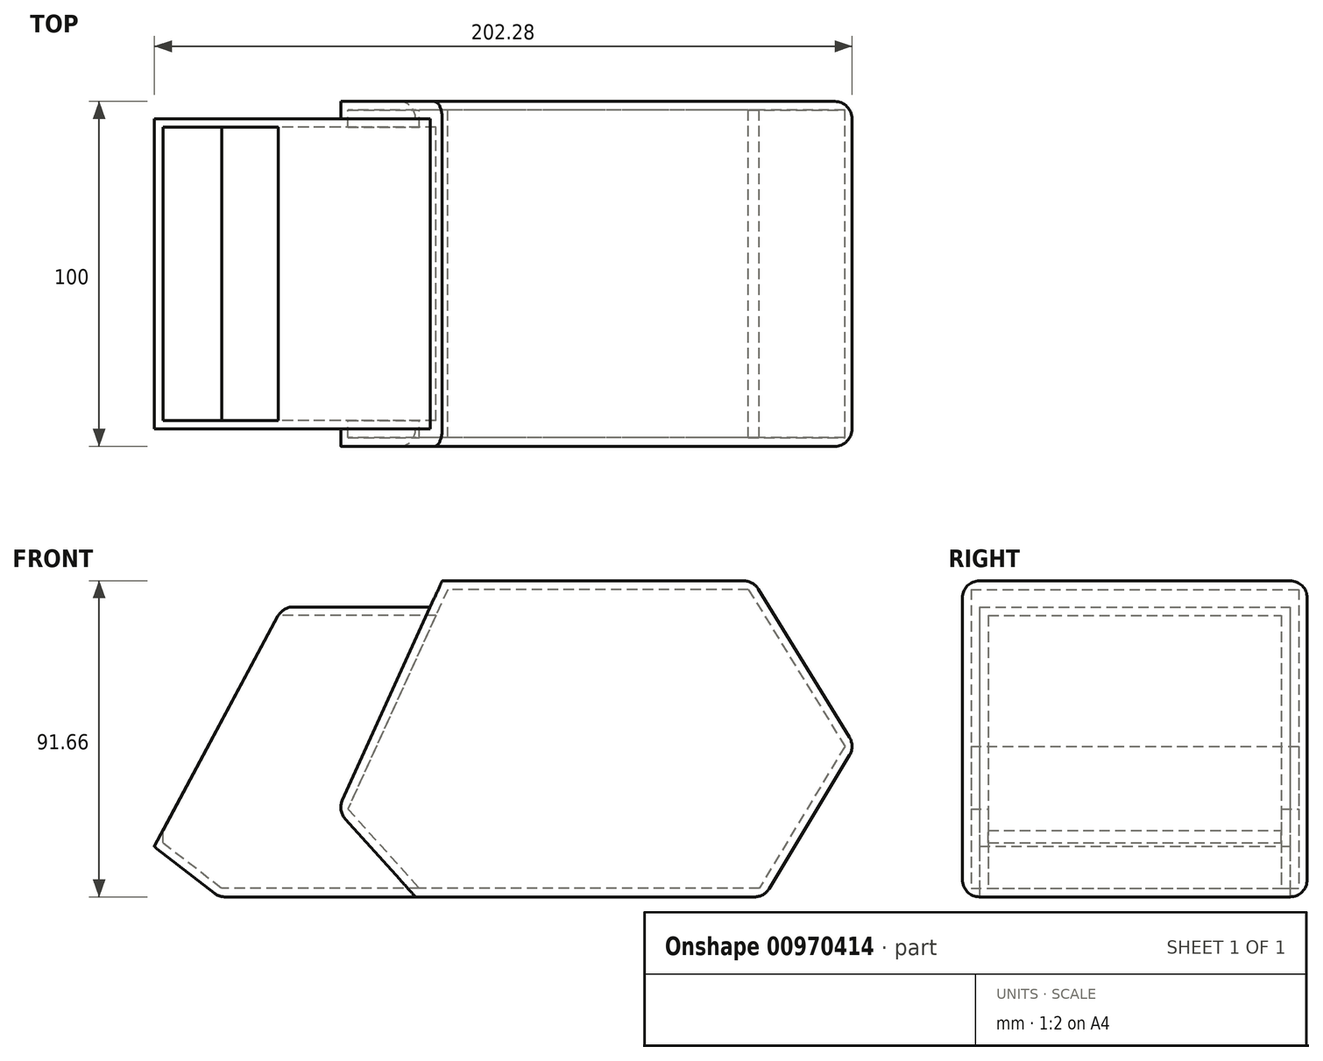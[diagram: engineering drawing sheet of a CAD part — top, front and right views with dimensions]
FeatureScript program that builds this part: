
annotation { "Feature Type Name" : "Feature", "Feature Type Description" : "" }
export const myFeature = defineFeature(function(context is Context, id is Id, definition is map)
    precondition{}
    {
        {
            var Q0;
            Q0=qCreatedBy(makeId("Front.planeOp"),FACE);
            var sketch = newSketch(context, id + "F0", { "sketchPlane" : qUnion([Q0])});
            skLineSegment(sketch, "E0.bottom", {"start": v(74.72, -45.83) * mm, "end": v(-83.37, -45.83) * mm});
            skLineSegment(sketch, "E0.top", {"start": v(71.54, 45.83) * mm, "end": v(-18.63, 45.83) * mm});
            skLineSegment(sketch, "E0.right", {"start": v(-102.1, -31.3) * mm, "end": v(-102.1, -31.17) * mm});
            skPoint(sketch, "E0.middle", {"position": v(0, 0) * mm});
            skLineSegment(sketch, "E1", {"start": v(-18.63, 45.83) * mm, "end": v(-48.93, -20.8) * mm});
            skLineSegment(sketch, "E2", {"start": v(-48.93, -20.8) * mm, "end": v(-26.37, -45.83) * mm});
            skLineSegment(sketch, "E3", {"start": v(71.54, 45.83) * mm, "end": v(101.05, -2.12) * mm});
            skLineSegment(sketch, "E4", {"start": v(101.05, -2.12) * mm, "end": v(74.72, -45.83) * mm});
            skPoint(sketch, "E5.orphan", {"position": v(102.1, 45.83) * mm});
            skPoint(sketch, "E6.orphan", {"position": v(102.1, -45.83) * mm});
            skLineSegment(sketch, "E7", {"start": v(-22.08, 38.24) * mm, "end": v(-64.83, 38.24) * mm});
            skPoint(sketch, "E8.orphan", {"position": v(-102.1, 45.83) * mm});
            skLineSegment(sketch, "E9", {"start": v(-64.83, 38.24) * mm, "end": v(-102.14, -31.27) * mm});
            skLineSegment(sketch, "E10", {"start": v(-102.14, -31.27) * mm, "end": v(-83.37, -45.83) * mm});
            skPoint(sketch, "E11.orphan", {"position": v(-102.1, -45.83) * mm});
            skSolve(sketch);
        }
        {
            var Q0;
            {var subQ1=sQuery(id+"F0.wireOp",EDGE,"E0.top");Q0=makeQuery(id+"F0.imprint","IMPRINT",FACE,{"disambiguationData":[TD([[makeQuery(id+"F0.imprint","IMPRINT",EDGE,{"derivedFrom":subQ1}),1.0]])]});}
            extrude(context, id + "F1", {"entities" : qUnion([Q0]), "depth" : 50 * mm, "offsetDistance" : 25 * mm, "hasSecondDirection" : true, "secondDirectionOppositeDirection" : true, "secondDirectionDepth" : 50 * mm});
        }
        {
            var Q0;
            {var subQ3=sQuery(id+"F0.wireOp",EDGE,"E0.right");Q0=makeQuery(id+"F0.imprint","IMPRINT",FACE,{"disambiguationData":[TD([[makeQuery(id+"F0.imprint","IMPRINT",EDGE,{"derivedFrom":subQ3}),-1.0]])]});}
            extrude(context, id + "F2", {"entities" : qUnion([Q0]), "operationType" : NewBodyOperationType.ADD, "depth" : 45 * mm, "offsetDistance" : 25 * mm, "hasSecondDirection" : true, "secondDirectionOppositeDirection" : true, "secondDirectionDepth" : 45 * mm});
        }
        {
            var Q0;
            Q0=makeQuery(id+"F2.opExtrude","SWEPT_FACE",FACE,{"disambiguationData":[OSD([sQuery(id+"F0.wireOp",EDGE,"E9")])]});
            shell(context, id + "F3", {"entities" : qUnion([Q0]), "thickness" : 2.5 * mm});
        }
        {
            var Q0;
            Q0=makeQuery(id+"F1.opExtrude","CAP_EDGE",EDGE,{"disambiguationData":[OSD([sQuery(id+"F0.wireOp",EDGE,"E0.top")])],"isStart":false});
            var Q1;
            Q1=makeQuery(id+"F1.opExtrude","CAP_EDGE",EDGE,{"disambiguationData":[OSD([sQuery(id+"F0.wireOp",EDGE,"E0.bottom")])],"isStart":false});
            var Q2;
            Q2=makeQuery(id+"F1.opExtrude","CAP_EDGE",EDGE,{"disambiguationData":[OSD([sQuery(id+"F0.wireOp",EDGE,"E0.top")])],"isStart":true});
            var Q3;
            Q3=makeQuery(id+"F1.opExtrude","CAP_EDGE",EDGE,{"disambiguationData":[OSD([sQuery(id+"F0.wireOp",EDGE,"E0.bottom")])],"isStart":true});
            var Q4;
            Q4=makeQuery(id+"F1.opExtrude","SWEPT_EDGE",EDGE,{"disambiguationData":[OSD([sQuery(id+"F0.wireOp",EDGE,"E0.top"),sQuery(id+"F0.wireOp",EDGE,"E3")])]});
            var Q5;
            Q5=makeQuery(id+"F1.opExtrude","SWEPT_EDGE",EDGE,{"disambiguationData":[OSD([sQuery(id+"F0.wireOp",EDGE,"E3"),sQuery(id+"F0.wireOp",EDGE,"E4")])]});
            var Q6;
            Q6=makeQuery(id+"F1.opExtrude","SWEPT_EDGE",EDGE,{"disambiguationData":[OSD([sQuery(id+"F0.wireOp",EDGE,"E0.bottom"),sQuery(id+"F0.wireOp",EDGE,"E4")])]});
            var Q7;
            Q7=makeQuery(id+"F1.opExtrude","CAP_EDGE",EDGE,{"disambiguationData":[OSD([sQuery(id+"F0.wireOp",EDGE,"E3")])],"isStart":false});
            var Q8;
            Q8=makeQuery(id+"F1.opExtrude","CAP_EDGE",EDGE,{"disambiguationData":[OSD([sQuery(id+"F0.wireOp",EDGE,"E4")])],"isStart":false});
            var Q9;
            Q9=makeQuery(id+"F1.opExtrude","CAP_EDGE",EDGE,{"disambiguationData":[OSD([sQuery(id+"F0.wireOp",EDGE,"E3")])],"isStart":true});
            var Q10;
            Q10=makeQuery(id+"F1.opExtrude","CAP_EDGE",EDGE,{"disambiguationData":[OSD([sQuery(id+"F0.wireOp",EDGE,"E4")])],"isStart":true});
            var Q11;
            {var subQ0=sQuery(id+"F0.wireOp",EDGE,"E2");var subQ1=sQuery(id+"F0.wireOp",EDGE,"E1");var subQ2=sQuery(id+"F0.wireOp",EDGE,"E0.bottom");Q11=makeQuery(id+"F2.boolean.opBoolean","SPLIT",EDGE,{"disambiguationData":[TD([makeQuery(id+"F1.opExtrude","CAP_FACE",FACE,{"disambiguationData":[OSD([subQ2,sQuery(id+"F0.wireOp",EDGE,"E0.top"),subQ1,subQ0,sQuery(id+"F0.wireOp",EDGE,"E3"),sQuery(id+"F0.wireOp",EDGE,"E4")])],"isStart":true})])],"derivedFrom":makeQuery(id+"F1.opExtrude","SWEPT_EDGE",EDGE,{"disambiguationData":[OSD([subQ1,subQ0])]})});}
            var Q12;
            {var subQ0=sQuery(id+"F0.wireOp",EDGE,"E2");var subQ1=sQuery(id+"F0.wireOp",EDGE,"E1");var subQ2=sQuery(id+"F0.wireOp",EDGE,"E0.bottom");Q12=makeQuery(id+"F2.boolean.opBoolean","SPLIT",EDGE,{"disambiguationData":[TD([makeQuery(id+"F1.opExtrude","CAP_FACE",FACE,{"disambiguationData":[OSD([subQ2,sQuery(id+"F0.wireOp",EDGE,"E0.top"),subQ1,subQ0,sQuery(id+"F0.wireOp",EDGE,"E3"),sQuery(id+"F0.wireOp",EDGE,"E4")])],"isStart":false})])],"derivedFrom":makeQuery(id+"F1.opExtrude","SWEPT_EDGE",EDGE,{"disambiguationData":[OSD([subQ1,subQ0])]})});}
            var Q13;
            Q13=makeQuery(id+"F2.opExtrude","SWEPT_EDGE",EDGE,{"disambiguationData":[OSD([sQuery(id+"F0.wireOp",EDGE,"E0.right"),sQuery(id+"F0.wireOp",EDGE,"E10")])]});
            var Q14;
            Q14=makeQuery(id+"F2.opExtrude","SWEPT_EDGE",EDGE,{"disambiguationData":[OSD([sQuery(id+"F0.wireOp",EDGE,"E7"),sQuery(id+"F0.wireOp",EDGE,"E9")])]});
            var Q15;
            Q15=makeQuery(id+"F2.opExtrude","SWEPT_EDGE",EDGE,{"disambiguationData":[OSD([sQuery(id+"F0.wireOp",EDGE,"E0.bottom"),sQuery(id+"F0.wireOp",EDGE,"E10")])]});
            fillet(context, id + "F4", {"entities" : qUnion([Q0, Q1, Q2, Q3, Q4, Q5, Q6, Q7, Q8, Q9, Q10, Q11, Q12, Q13, Q14, Q15]), "radius" : 5 * mm, "tangentPropagation" : true, "allowEdgeOverflow" : false});
        }
    });
